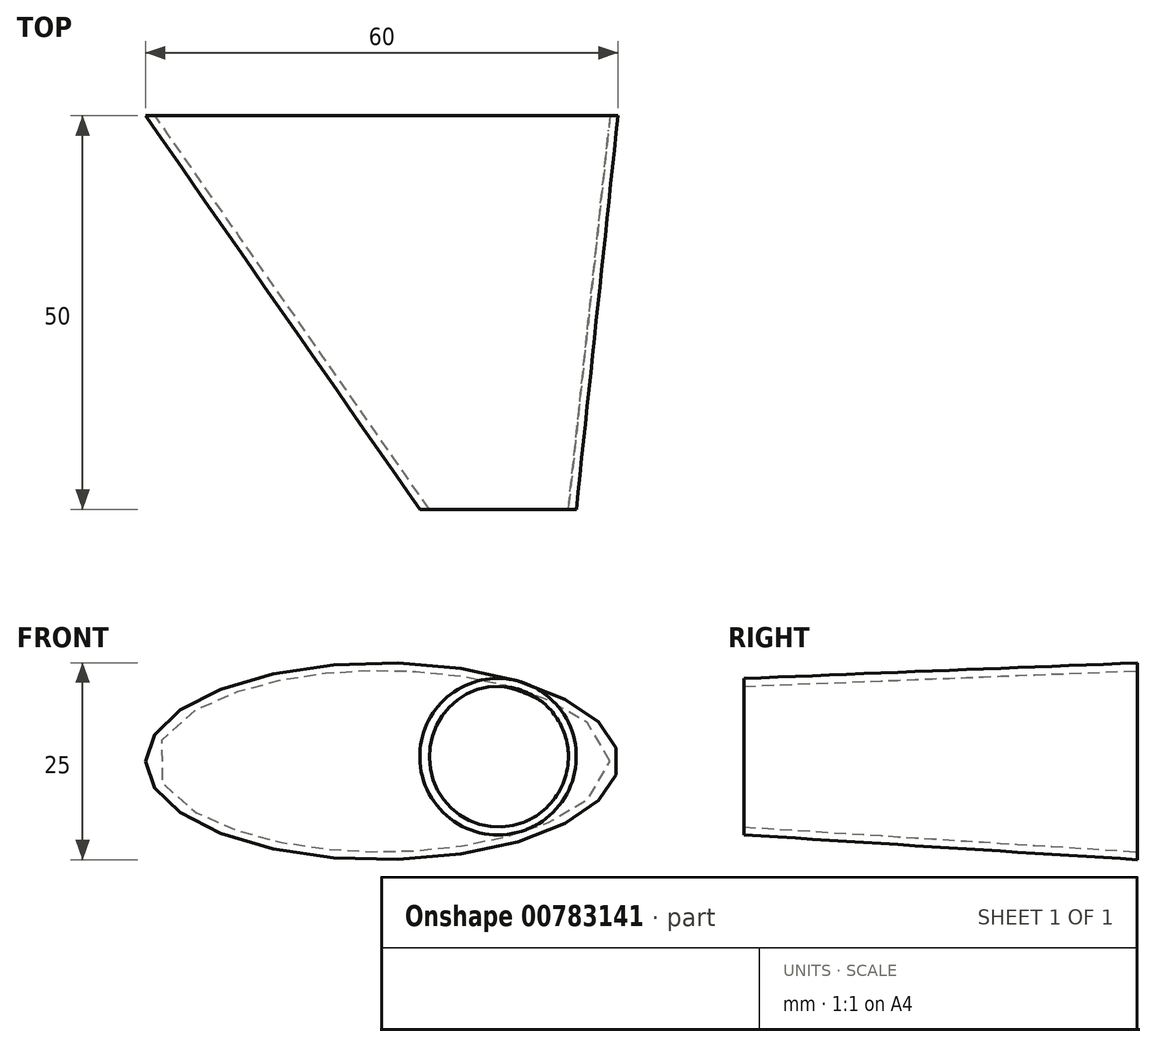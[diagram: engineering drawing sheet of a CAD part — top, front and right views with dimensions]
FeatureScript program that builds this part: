
annotation { "Feature Type Name" : "Feature", "Feature Type Description" : "" }
export const myFeature = defineFeature(function(context is Context, id is Id, definition is map)
    precondition{}
    {
        {
            var Q0;
            Q0=qCreatedBy(makeId("Front.planeOp"),FACE);
            cPlane(context, id + "F0", {"entities" : qUnion([Q0]), "cplaneType" : CPlaneType.OFFSET, "offset" : 100 * mm, "width" : 150 * mm, "height" : 150 * mm});
        }
        {
            var Q0;
            Q0=qCreatedBy(id+"F0.planeOp",FACE);
            cPlane(context, id + "F1", {"entities" : qUnion([Q0]), "cplaneType" : CPlaneType.OFFSET, "offset" : 50 * mm, "width" : 150 * mm, "height" : 150 * mm});
        }
        {
            var Q0;
            Q0=qCreatedBy(id+"F0.planeOp",FACE);
            var sketch = newSketch(context, id + "F2", { "sketchPlane" : qUnion([Q0])});
            skEllipse(sketch, "E0", {"center": v(-27.91, 4.08) * mm, "majorRadius": 30 * mm, "minorRadius": 12.5 * mm, "majorAxis": v(-1, 0)});
            skSolve(sketch);
        }
        {
            var Q0;
            Q0=qCreatedBy(id+"F1.planeOp",FACE);
            var sketch = newSketch(context, id + "F3", { "sketchPlane" : qUnion([Q0])});
            skCircle(sketch, "E1", {"center": v(-13.14, 4.67) * mm, "radius": 9.94 * mm});
            skSolve(sketch);
        }
        {
            var Q0;
            Q0=makeQuery(id+"F2.imprint","IMPRINT",FACE,{"disambiguationData":[TD([[makeQuery(id+"F2.imprint","IMPRINT",EDGE,{"derivedFrom":sQuery(id+"F2.wireOp",EDGE,"E0")}),1.0]])]});
            var Q1;
            Q1=makeQuery(id+"F3.imprint","IMPRINT",FACE,{"disambiguationData":[TD([[makeQuery(id+"F3.imprint","IMPRINT",EDGE,{"derivedFrom":sQuery(id+"F3.wireOp",EDGE,"E1")}),1.0]])]});
            loft(context, id + "F4", {"sheetProfilesArray" : [{ "sheetProfileEntities" : qUnion([Q0]) }, { "sheetProfileEntities" : qUnion([Q1]) }]});
        }
        {
            var Q0;
            Q0=makeQuery(id+"F4.opLoft","CAP_FACE",FACE,{"disambiguationData":[OSD([makeQuery(id+"F3.imprint","IMPRINT",FACE,{"disambiguationData":[TD([[makeQuery(id+"F3.imprint","IMPRINT",EDGE,{"derivedFrom":sQuery(id+"F3.wireOp",EDGE,"E1")}),1.0]])]})])],"isStart":true});
            var Q1;
            Q1=makeQuery(id+"F4.opLoft","CAP_FACE",FACE,{"disambiguationData":[OSD([makeQuery(id+"F2.imprint","IMPRINT",FACE,{"disambiguationData":[TD([[makeQuery(id+"F2.imprint","IMPRINT",EDGE,{"derivedFrom":sQuery(id+"F2.wireOp",EDGE,"E0")}),1.0]])]})])],"isStart":true});
            shell(context, id + "F5", {"entities" : qUnion([Q0, Q1]), "thickness" : 1 * mm});
        }
    });
